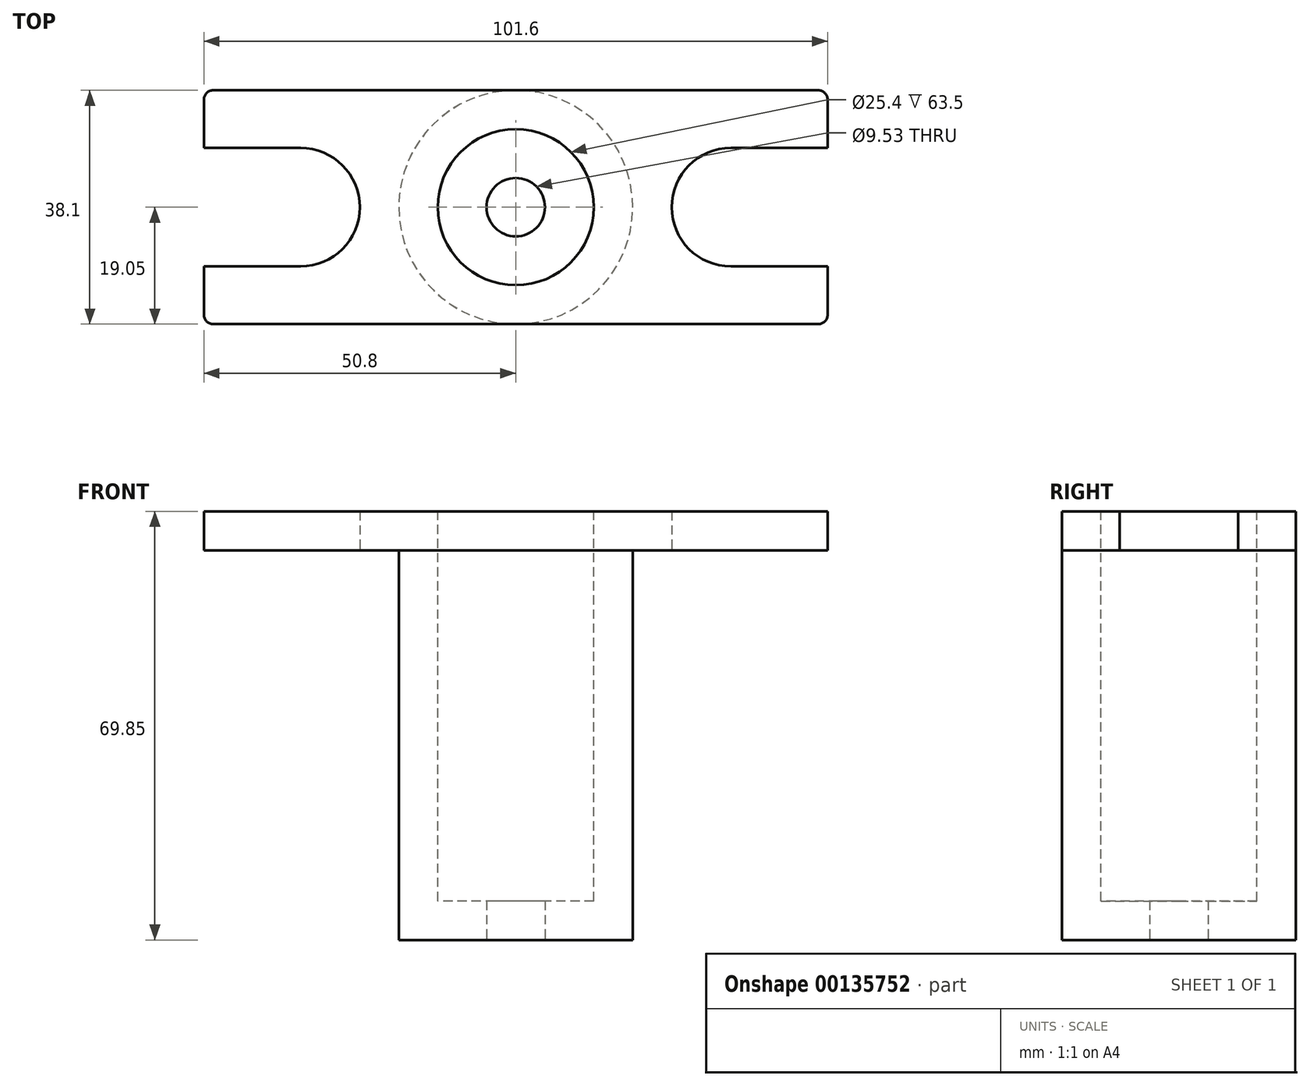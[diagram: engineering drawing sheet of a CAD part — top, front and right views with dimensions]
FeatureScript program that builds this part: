
annotation { "Feature Type Name" : "Feature", "Feature Type Description" : "" }
export const myFeature = defineFeature(function(context is Context, id is Id, definition is map)
    precondition{}
    {
        {
            var Q0;
            Q0=qCreatedBy(makeId("Top.planeOp"),FACE);
            var sketch = newSketch(context, id + "F0", { "sketchPlane" : qUnion([Q0])});
            skLineSegment(sketch, "E0", {"start": v(0, 0) * mm, "end": v(101.6, 0) * mm});
            skLineSegment(sketch, "E1", {"start": v(0, 38.1) * mm, "end": v(101.6, 38.1) * mm});
            skLineSegment(sketch, "E2", {"start": v(101.6, 28.7) * mm, "end": v(85.85, 28.7) * mm});
            skLineSegment(sketch, "E3", {"start": v(101.6, 9.4) * mm, "end": v(85.85, 9.4) * mm});
            skLineSegment(sketch, "E4", {"start": v(0, 9.4) * mm, "end": v(15.75, 9.4) * mm});
            skLineSegment(sketch, "E5", {"start": v(0, 28.7) * mm, "end": v(15.75, 28.7) * mm});
            skArc(sketch, "E6", {"start": v(15.75, 28.7) * mm, "mid": v(25.4, 19.05) * mm, "end": v(15.75, 9.4) * mm});
            skArc(sketch, "E7", {"start": v(85.85, 28.7) * mm, "mid": v(76.2, 19.05) * mm, "end": v(85.85, 9.4) * mm});
            skLineSegment(sketch, "E8", {"start": v(0, 28.7) * mm, "end": v(0, 38.1) * mm});
            skLineSegment(sketch, "E9", {"start": v(0, 9.4) * mm, "end": v(0, 0) * mm});
            skLineSegment(sketch, "E10", {"start": v(101.6, 0) * mm, "end": v(101.6, 9.4) * mm});
            skLineSegment(sketch, "E11", {"start": v(101.6, 28.7) * mm, "end": v(101.6, 38.1) * mm});
            skSolve(sketch);
        }
        {
            var Q0;
            Q0 = qSketchRegion(id + "F0", true);
            extrude(context, id + "F1", {"entities" : qUnion([Q0]), "depth" : 6.35 * mm});
        }
        {
            var Q0;
            Q0=makeQuery(id+"F1.opExtrude","SWEPT_EDGE",EDGE,{"disambiguationData":[OSD([sQuery(id+"F0.wireOp",EDGE,"E0"),sQuery(id+"F0.wireOp",EDGE,"E10")])]});
            fillet(context, id + "F2", {"entities" : qUnion([Q0]), "radius" : 1.52 * mm, "tangentPropagation" : true, "allowEdgeOverflow" : false});
        }
        {
            var Q0;
            Q0=makeQuery(id+"F1.opExtrude","SWEPT_EDGE",EDGE,{"disambiguationData":[OSD([sQuery(id+"F0.wireOp",EDGE,"E1"),sQuery(id+"F0.wireOp",EDGE,"E11")])]});
            fillet(context, id + "F3", {"entities" : qUnion([Q0]), "radius" : 1.52 * mm, "tangentPropagation" : true, "allowEdgeOverflow" : false});
        }
        {
            var Q0;
            Q0=makeQuery(id+"F1.opExtrude","SWEPT_EDGE",EDGE,{"disambiguationData":[OSD([sQuery(id+"F0.wireOp",EDGE,"E0"),sQuery(id+"F0.wireOp",EDGE,"E9")])]});
            fillet(context, id + "F4", {"entities" : qUnion([Q0]), "radius" : 1.52 * mm, "tangentPropagation" : true, "allowEdgeOverflow" : false});
        }
        {
            var Q0;
            Q0=makeQuery(id+"F1.opExtrude","SWEPT_EDGE",EDGE,{"disambiguationData":[OSD([sQuery(id+"F0.wireOp",EDGE,"E1"),sQuery(id+"F0.wireOp",EDGE,"E8")])]});
            fillet(context, id + "F5", {"entities" : qUnion([Q0]), "radius" : 1.52 * mm, "tangentPropagation" : true, "allowEdgeOverflow" : false});
        }
        {
            var Q0;
            Q0=makeQuery(id+"F1.opExtrude","CAP_FACE",FACE,{"disambiguationData":[OSD([sQuery(id+"F0.wireOp",EDGE,"E0"),sQuery(id+"F0.wireOp",EDGE,"E1"),sQuery(id+"F0.wireOp",EDGE,"E2"),sQuery(id+"F0.wireOp",EDGE,"E3"),sQuery(id+"F0.wireOp",EDGE,"E4"),sQuery(id+"F0.wireOp",EDGE,"E5"),sQuery(id+"F0.wireOp",EDGE,"E6"),sQuery(id+"F0.wireOp",EDGE,"E7"),sQuery(id+"F0.wireOp",EDGE,"E8"),sQuery(id+"F0.wireOp",EDGE,"E9"),sQuery(id+"F0.wireOp",EDGE,"E10"),sQuery(id+"F0.wireOp",EDGE,"E11")])],"isStart":true});
            var sketch = newSketch(context, id + "F6", { "sketchPlane" : qUnion([Q0])});
            skCircle(sketch, "E12", {"center": v(50.8, -19.05) * mm, "radius": 19.05 * mm});
            skPoint(sketch, "E12.centerSnap0", {"position": v(50.8, 0) * mm});
            skPoint(sketch, "E12.centerSnap1", {"position": v(25.4, -19.05) * mm});
            skSolve(sketch);
        }
        {
            var Q0;
            Q0 = qSketchRegion(id + "F6", true);
            extrude(context, id + "F7", {"entities" : qUnion([Q0]), "operationType" : NewBodyOperationType.ADD, "depth" : 63.5 * mm});
        }
        {
            var Q0;
            Q0=makeQuery(id+"F1.opExtrude","CAP_FACE",FACE,{"disambiguationData":[OSD([sQuery(id+"F0.wireOp",EDGE,"E0"),sQuery(id+"F0.wireOp",EDGE,"E1"),sQuery(id+"F0.wireOp",EDGE,"E2"),sQuery(id+"F0.wireOp",EDGE,"E3"),sQuery(id+"F0.wireOp",EDGE,"E4"),sQuery(id+"F0.wireOp",EDGE,"E5"),sQuery(id+"F0.wireOp",EDGE,"E6"),sQuery(id+"F0.wireOp",EDGE,"E7"),sQuery(id+"F0.wireOp",EDGE,"E8"),sQuery(id+"F0.wireOp",EDGE,"E9"),sQuery(id+"F0.wireOp",EDGE,"E10"),sQuery(id+"F0.wireOp",EDGE,"E11")])],"isStart":false});
            var sketch = newSketch(context, id + "F8", { "sketchPlane" : qUnion([Q0])});
            skCircle(sketch, "E13", {"center": v(50.8, 19.05) * mm, "radius": 12.7 * mm});
            skPoint(sketch, "E13.centerSnap0", {"position": v(50.8, 38.1) * mm});
            skPoint(sketch, "E13.centerSnap1", {"position": v(25.4, 19.05) * mm});
            skSolve(sketch);
        }
        {
            var Q0;
            Q0 = qSketchRegion(id + "F8", true);
            extrude(context, id + "F9", {"entities" : qUnion([Q0]), "operationType" : NewBodyOperationType.REMOVE, "oppositeDirection" : true, "depth" : 63.5 * mm});
        }
        {
            var Q0;
            Q0=makeQuery(id+"F7.opExtrude","CAP_FACE",FACE,{"disambiguationData":[OSD([sQuery(id+"F6.wireOp",EDGE,"E12")])],"isStart":false});
            var sketch = newSketch(context, id + "F10", { "sketchPlane" : qUnion([Q0])});
            skCircle(sketch, "E14", {"center": v(50.8, -19.05) * mm, "radius": 4.76 * mm});
            skSolve(sketch);
        }
        {
            var Q0;
            Q0 = qSketchRegion(id + "F10", true);
            extrude(context, id + "F11", {"entities" : qUnion([Q0]), "operationType" : NewBodyOperationType.REMOVE, "endBound" : BoundingType.THROUGH_ALL, "oppositeDirection" : true, "depth" : 25.4 * mm});
        }
    });
